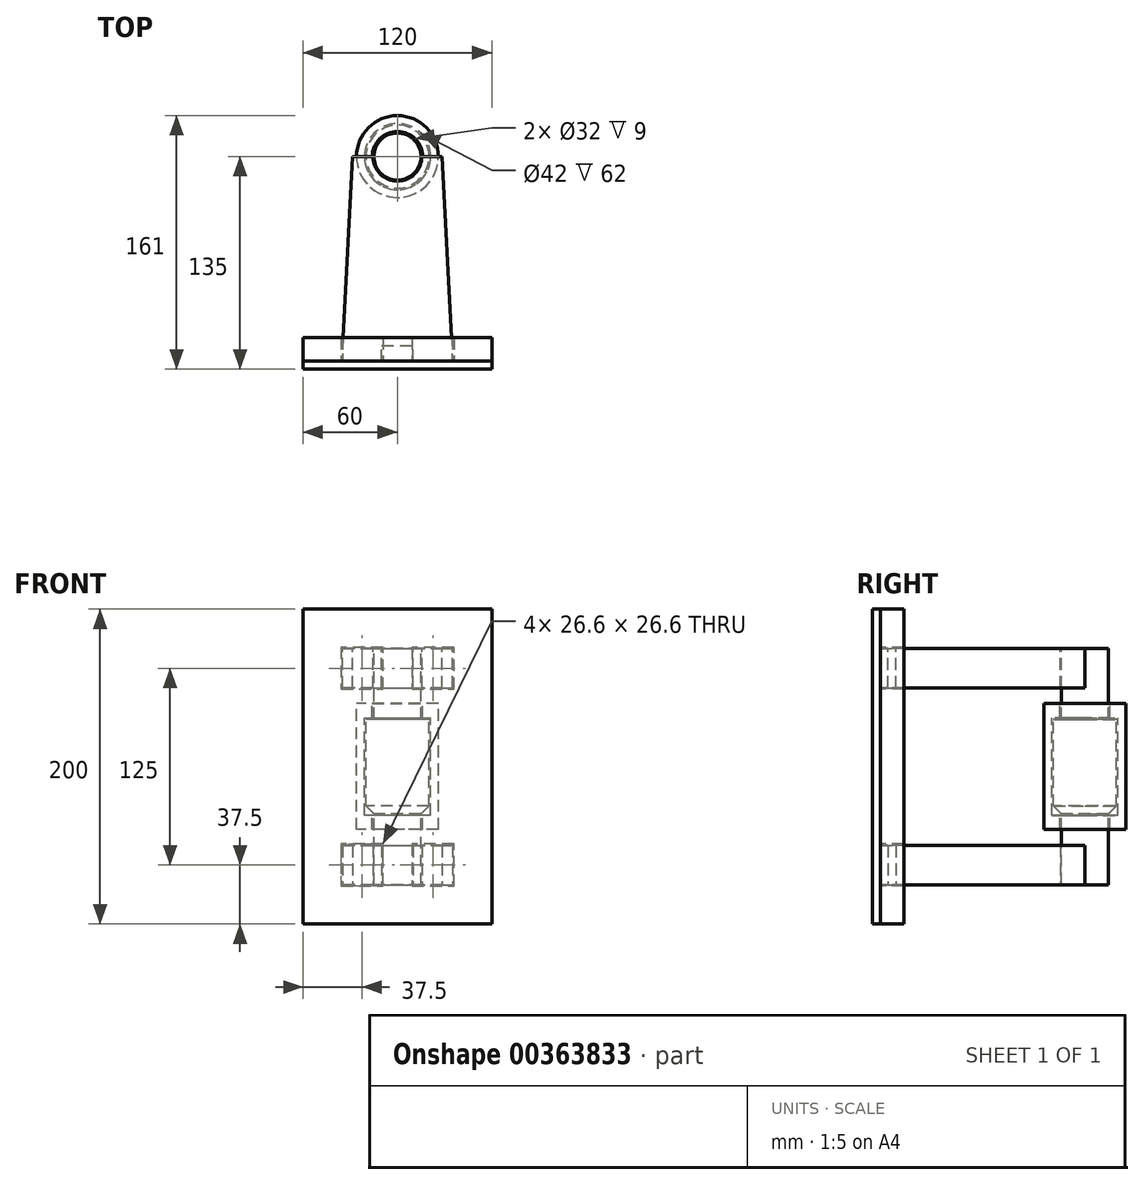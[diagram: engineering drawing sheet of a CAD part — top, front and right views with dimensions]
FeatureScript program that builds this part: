
annotation { "Feature Type Name" : "Feature", "Feature Type Description" : "" }
export const myFeature = defineFeature(function(context is Context, id is Id, definition is map)
    precondition{}
    {
        {
            var Q0;
            Q0=qCreatedBy(makeId("Front.planeOp"),FACE);
            var sketch = newSketch(context, id + "F0", { "sketchPlane" : qUnion([Q0])});
            skLineSegment(sketch, "E0", {"start": v(0, 0) * mm, "end": v(26, 0) * mm});
            skLineSegment(sketch, "E1", {"start": v(26, 0) * mm, "end": v(26, 80) * mm});
            skLineSegment(sketch, "E2", {"start": v(26, 80) * mm, "end": v(0, 80) * mm});
            skLineSegment(sketch, "E3", {"start": v(0, 80) * mm, "end": v(0, 0) * mm});
            skSolve(sketch);
        }
        {
            var Q0;
            Q0=qCreatedBy(makeId("Front.planeOp"),FACE);
            var sketch = newSketch(context, id + "F1", { "sketchPlane" : qUnion([Q0])});
            skLineSegment(sketch, "E4", {"start": v(0, 0) * mm, "end": v(15.4, 0) * mm});
            skLineSegment(sketch, "E5", {"start": v(15, 10) * mm, "end": v(20, 10) * mm});
            skLineSegment(sketch, "E6", {"start": v(20, 10) * mm, "end": v(20, 70) * mm});
            skLineSegment(sketch, "E7", {"start": v(20, 70) * mm, "end": v(15, 70) * mm});
            skLineSegment(sketch, "E8", {"start": v(0, 115) * mm, "end": v(0, -35) * mm});
            skLineSegment(sketch, "E9", {"start": v(0, 115) * mm, "end": v(15, 115) * mm});
            skLineSegment(sketch, "E10", {"start": v(15, 115) * mm, "end": v(15, 70) * mm});
            skLineSegment(sketch, "E11", {"start": v(15, -35) * mm, "end": v(0, -35) * mm});
            skPoint(sketch, "E12.0.end.orphan", {"position": v(0, 80) * mm});
            skLineSegment(sketch, "E13.trimOffspring", {"start": v(15, 10) * mm, "end": v(15, -35) * mm});
            skSolve(sketch);
        }
        {
            var Q0;
            Q0=qSketchRegion(id+"F0",true);
            var Q1;
            Q1=sQuery(id+"F1.wireOp",EDGE,"E8");
            revolve(context, id + "F2", {"entities" : qUnion([Q0]), "axis" : qUnion([Q1]), "revolveType" : RevolveType.FULL});
        }
        {
            var Q0;
            Q0=qSketchRegion(id+"F1",true);
            var Q1;
            Q1=sQuery(id+"F1.wireOp",EDGE,"E8");
            revolve(context, id + "F3", {"entities" : qUnion([Q0]), "axis" : qUnion([Q1]), "revolveType" : RevolveType.FULL});
        }
        {
            var Q0;
            Q0=makeQuery(id+"F3.opRevolve","SWEPT_BODY",BODY,{"disambiguationData":[OSD([sQuery(id+"F1.wireOp",EDGE,"E5"),sQuery(id+"F1.wireOp",EDGE,"E6"),sQuery(id+"F1.wireOp",EDGE,"E7"),sQuery(id+"F1.wireOp",EDGE,"E8"),sQuery(id+"F1.wireOp",EDGE,"E9"),sQuery(id+"F1.wireOp",EDGE,"E10"),sQuery(id+"F1.wireOp",EDGE,"E11"),sQuery(id+"F1.wireOp",EDGE,"E13.trimOffspring")])]});
            var Q1;
            Q1=makeQuery(id+"F2.opRevolve","SWEPT_BODY",BODY,{"disambiguationData":[OSD([sQuery(id+"F0.wireOp",EDGE,"E0"),sQuery(id+"F0.wireOp",EDGE,"E1"),sQuery(id+"F0.wireOp",EDGE,"E2"),sQuery(id+"F0.wireOp",EDGE,"E3")])]});
            booleanBodies(context, id + "F4", {"operationType" : BooleanOperationType.SUBTRACTION, "tools" : qUnion([Q0]), "targets" : qUnion([Q1]), "offset" : true, "offsetAll" : true, "offsetDistance" : 1 * mm, "keepTools" : true});
        }
        {
            var Q0;
            Q0=makeQuery(id+"F3.opRevolve","SWEPT_EDGE",EDGE,{"disambiguationData":[OSD([sQuery(id+"F1.wireOp",EDGE,"E5"),sQuery(id+"F1.wireOp",EDGE,"E6")])]});
            chamfer(context, id + "F5", {"entities" : qUnion([Q0]), "width" : 5 * mm, "tangentPropagation" : true});
        }
        {
            var Q0;
            Q0=makeQuery(id+"F3.opRevolve","SWEPT_FACE",FACE,{"disambiguationData":[OSD([sQuery(id+"F1.wireOp",EDGE,"E9")])]});
            var sketch = newSketch(context, id + "F6", { "sketchPlane" : qUnion([Q0])});
            skLineSegment(sketch, "E14", {"start": v(0, 0) * mm, "end": v(-15, 0) * mm});
            skLineSegment(sketch, "E15", {"start": v(0, 0) * mm, "end": v(15, 0) * mm});
            skLineSegment(sketch, "E16", {"start": v(-15, 0) * mm, "end": v(-35, 0) * mm});
            skLineSegment(sketch, "E17", {"start": v(-35, 0) * mm, "end": v(-35, -130) * mm});
            skLineSegment(sketch, "E18", {"start": v(-35, -130) * mm, "end": v(35, -130) * mm});
            skLineSegment(sketch, "E19", {"start": v(35, -130) * mm, "end": v(35, 0) * mm});
            skLineSegment(sketch, "E20", {"start": v(35, 0) * mm, "end": v(0, 0) * mm});
            skLineSegment(sketch, "E21", {"start": v(28.43, 0) * mm, "end": v(35, -125.14) * mm});
            skLineSegment(sketch, "E22", {"start": v(-28.43, 0) * mm, "end": v(-35, -125.14) * mm});
            skLineSegment(sketch, "E23", {"start": v(0, 0) * mm, "end": v(0, -116.48) * mm, "construction": true});
            skLineSegment(sketch, "E24.bottom", {"start": v(-10, -130) * mm, "end": v(10, -130) * mm});
            skLineSegment(sketch, "E24.top", {"start": v(-10, -120) * mm, "end": v(10, -120) * mm});
            skLineSegment(sketch, "E24.left", {"start": v(-10, -130) * mm, "end": v(-10, -120) * mm});
            skLineSegment(sketch, "E24.right", {"start": v(10, -130) * mm, "end": v(10, -120) * mm});
            skSolve(sketch);
        }
        {
            var Q0;
            {var subQ0=sQuery(id+"F6.wireOp",EDGE,"E18");Q0=makeQuery(id+"F6.imprint","IMPRINT",FACE,{"disambiguationData":[TD([[makeQuery(id+"F6.imprint","IMPRINT",EDGE,{"derivedFrom":subQ0}),1.0]])]});}
            var Q1;
            {var subQ0=sQuery(id+"F6.wireOp",EDGE,"E14");Q1=makeQuery(id+"F6.imprint","IMPRINT",FACE,{"disambiguationData":[TD([[makeQuery(id+"F6.imprint","IMPRINT",EDGE,{"derivedFrom":subQ0}),1.0]])]});}
            extrude(context, id + "F7", {"entities" : qUnion([Q0, Q1]), "oppositeDirection" : true, "depth" : 25 * mm});
        }
        {
            var Q0;
            Q0=makeQuery(id+"F3.opRevolve","SWEPT_BODY",BODY,{"disambiguationData":[OSD([sQuery(id+"F1.wireOp",EDGE,"E5"),sQuery(id+"F1.wireOp",EDGE,"E6"),sQuery(id+"F1.wireOp",EDGE,"E7"),sQuery(id+"F1.wireOp",EDGE,"E8"),sQuery(id+"F1.wireOp",EDGE,"E9"),sQuery(id+"F1.wireOp",EDGE,"E10"),sQuery(id+"F1.wireOp",EDGE,"E11"),sQuery(id+"F1.wireOp",EDGE,"E13.trimOffspring")])]});
            var Q1;
            Q1=makeQuery(id+"F7.opExtrude","SWEPT_BODY",BODY,{"disambiguationData":[OSD([sQuery(id+"F6.wireOp",EDGE,"E14"),sQuery(id+"F6.wireOp",EDGE,"E16"),sQuery(id+"F6.wireOp",EDGE,"E17"),sQuery(id+"F6.wireOp",EDGE,"E18"),sQuery(id+"F6.wireOp",EDGE,"E19"),sQuery(id+"F6.wireOp",EDGE,"E20"),sQuery(id+"F6.wireOp",EDGE,"E21"),sQuery(id+"F6.wireOp",EDGE,"E22")])]});
            booleanBodies(context, id + "F8", {"operationType" : BooleanOperationType.SUBTRACTION, "tools" : qUnion([Q0]), "targets" : qUnion([Q1]), "offset" : true, "offsetAll" : true, "offsetDistance" : .5 * mm, "keepTools" : true});
        }
        {
            var Q0;
            Q0=qCreatedBy(makeId("Top.planeOp"),FACE);
            cPlane(context, id + "F9", {"entities" : qUnion([Q0]), "cplaneType" : CPlaneType.OFFSET, "offset" : 40 * mm, "width" : 150 * mm, "height" : 150 * mm});
        }
        {
            var Q0;
            Q0=makeQuery(id+"F7.opExtrude","SWEPT_BODY",BODY,{"disambiguationData":[OSD([sQuery(id+"F6.wireOp",EDGE,"E14"),sQuery(id+"F6.wireOp",EDGE,"E16"),sQuery(id+"F6.wireOp",EDGE,"E17"),sQuery(id+"F6.wireOp",EDGE,"E18"),sQuery(id+"F6.wireOp",EDGE,"E19"),sQuery(id+"F6.wireOp",EDGE,"E20"),sQuery(id+"F6.wireOp",EDGE,"E21"),sQuery(id+"F6.wireOp",EDGE,"E22"),sQuery(id+"F6.wireOp",EDGE,"E24.top"),sQuery(id+"F6.wireOp",EDGE,"E24.left"),sQuery(id+"F6.wireOp",EDGE,"E24.right")])]});
            var Q1;
            Q1=qCreatedBy(id+"F9.planeOp",FACE);
            mirror(context, id + "F10", {"entities" : qUnion([Q0]), "mirrorPlane" : qUnion([Q1])});
        }
        {
            var Q0;
            {var subQ0=sQuery(id+"F6.wireOp",EDGE,"E18");Q0=makeQuery(id+"F7.opExtrude","SWEPT_FACE",FACE,{"disambiguationData":[OSD([subQ0]),TDD([makeQuery(id+"F6.imprint","IMPRINT",EDGE,{"disambiguationData":[TD([[makeQuery(id+"F6.imprint","INTERSECT",VERTEX,{"derivedFrom":[subQ0,sQuery(id+"F6.wireOp",EDGE,"E19")]}),1.0]])],"derivedFrom":subQ0})])]});}
            var sketch = newSketch(context, id + "F11", { "sketchPlane" : qUnion([Q0])});
            skPoint(sketch, "E25.0", {"position": v(0, 40) * mm});
            skLineSegment(sketch, "E26.bottom", {"start": v(-60, 140) * mm, "end": v(60, 140) * mm});
            skLineSegment(sketch, "E26.top", {"start": v(-60, -60) * mm, "end": v(60, -60) * mm});
            skLineSegment(sketch, "E26.left", {"start": v(-60, 140) * mm, "end": v(-60, -60) * mm});
            skLineSegment(sketch, "E26.right", {"start": v(60, 140) * mm, "end": v(60, -60) * mm});
            skLineSegment(sketch, "E27.0.0", {"start": v(-10, 115) * mm, "end": v(-35, 115) * mm});
            skLineSegment(sketch, "E27.0.1", {"start": v(-35, 115) * mm, "end": v(-35, 90) * mm});
            skLineSegment(sketch, "E27.0.2", {"start": v(-35, 90) * mm, "end": v(-10, 90) * mm});
            skLineSegment(sketch, "E27.0.3", {"start": v(-10, 90) * mm, "end": v(-10, 115) * mm});
            skLineSegment(sketch, "E28.0.0", {"start": v(35, 115) * mm, "end": v(10, 115) * mm});
            skLineSegment(sketch, "E28.0.1", {"start": v(10, 115) * mm, "end": v(10, 90) * mm});
            skLineSegment(sketch, "E28.0.2", {"start": v(10, 90) * mm, "end": v(35, 90) * mm});
            skLineSegment(sketch, "E28.0.3", {"start": v(35, 90) * mm, "end": v(35, 115) * mm});
            skLineSegment(sketch, "E29.0.0", {"start": v(10, -35) * mm, "end": v(35, -35) * mm});
            skLineSegment(sketch, "E29.0.1", {"start": v(35, -35) * mm, "end": v(35, -10) * mm});
            skLineSegment(sketch, "E29.0.2", {"start": v(35, -10) * mm, "end": v(10, -10) * mm});
            skLineSegment(sketch, "E29.0.3", {"start": v(10, -10) * mm, "end": v(10, -35) * mm});
            skLineSegment(sketch, "E30.0.0", {"start": v(-35, -35) * mm, "end": v(-10, -35) * mm});
            skLineSegment(sketch, "E30.0.1", {"start": v(-10, -35) * mm, "end": v(-10, -10) * mm});
            skLineSegment(sketch, "E30.0.2", {"start": v(-10, -10) * mm, "end": v(-35, -10) * mm});
            skLineSegment(sketch, "E30.0.3", {"start": v(-35, -10) * mm, "end": v(-35, -35) * mm});
            skLineSegment(sketch, "E31.0", {"start": v(-9.2, 89.2) * mm, "end": v(-9.2, 115.8) * mm});
            skLineSegment(sketch, "E31.1", {"start": v(-35.8, 89.2) * mm, "end": v(-9.2, 89.2) * mm});
            skLineSegment(sketch, "E31.2", {"start": v(-35.8, 115.8) * mm, "end": v(-35.8, 89.2) * mm});
            skLineSegment(sketch, "E31.3", {"start": v(-9.2, 115.8) * mm, "end": v(-35.8, 115.8) * mm});
            skLineSegment(sketch, "E32.0", {"start": v(9.2, 115.8) * mm, "end": v(9.2, 89.2) * mm});
            skLineSegment(sketch, "E32.1", {"start": v(35.8, 115.8) * mm, "end": v(9.2, 115.8) * mm});
            skLineSegment(sketch, "E32.2", {"start": v(35.8, 89.2) * mm, "end": v(35.8, 115.8) * mm});
            skLineSegment(sketch, "E32.3", {"start": v(9.2, 89.2) * mm, "end": v(35.8, 89.2) * mm});
            skLineSegment(sketch, "E33.0", {"start": v(9.2, -9.2) * mm, "end": v(9.2, -35.8) * mm});
            skLineSegment(sketch, "E33.1", {"start": v(35.8, -9.2) * mm, "end": v(9.2, -9.2) * mm});
            skLineSegment(sketch, "E33.2", {"start": v(35.8, -35.8) * mm, "end": v(35.8, -9.2) * mm});
            skLineSegment(sketch, "E33.3", {"start": v(9.2, -35.8) * mm, "end": v(35.8, -35.8) * mm});
            skLineSegment(sketch, "E34.0", {"start": v(-35.8, -35.8) * mm, "end": v(-9.2, -35.8) * mm});
            skLineSegment(sketch, "E34.1", {"start": v(-35.8, -9.2) * mm, "end": v(-35.8, -35.8) * mm});
            skLineSegment(sketch, "E34.2", {"start": v(-9.2, -9.2) * mm, "end": v(-35.8, -9.2) * mm});
            skLineSegment(sketch, "E34.3", {"start": v(-9.2, -35.8) * mm, "end": v(-9.2, -9.2) * mm});
            skSolve(sketch);
        }
        {
            var Q0;
            Q0=makeQuery(id+"F11.imprint","IMPRINT",FACE,{"disambiguationData":[TD([[makeQuery(id+"F11.imprint","IMPRINT",EDGE,{"derivedFrom":sQuery(id+"F11.wireOp",EDGE,"E26.bottom")}),-1.0]])]});
            extrude(context, id + "F12", {"entities" : qUnion([Q0]), "oppositeDirection" : true, "depth" : 15 * mm});
        }
        {
            var Q0;
            Q0=makeQuery(id+"F11.imprint","IMPRINT",FACE,{"disambiguationData":[TD([[makeQuery(id+"F11.imprint","IMPRINT",EDGE,{"derivedFrom":sQuery(id+"F11.wireOp",EDGE,"E26.bottom")}),-1.0]])]});
            var Q1;
            Q1=makeQuery(id+"F11.imprint","IMPRINT",FACE,{"disambiguationData":[TD([[makeQuery(id+"F11.imprint","IMPRINT",EDGE,{"derivedFrom":sQuery(id+"F11.wireOp",EDGE,"E27.0.0")}),1.0]])]});
            var Q2;
            Q2=makeQuery(id+"F11.imprint","IMPRINT",FACE,{"disambiguationData":[TD([[makeQuery(id+"F11.imprint","IMPRINT",EDGE,{"derivedFrom":sQuery(id+"F11.wireOp",EDGE,"E28.0.0")}),-1.0]])]});
            var Q3;
            Q3=makeQuery(id+"F11.imprint","IMPRINT",FACE,{"disambiguationData":[TD([[makeQuery(id+"F11.imprint","IMPRINT",EDGE,{"derivedFrom":sQuery(id+"F11.wireOp",EDGE,"E29.0.0")}),1.0]])]});
            var Q4;
            Q4=makeQuery(id+"F11.imprint","IMPRINT",FACE,{"disambiguationData":[TD([[makeQuery(id+"F11.imprint","IMPRINT",EDGE,{"derivedFrom":sQuery(id+"F11.wireOp",EDGE,"E30.0.0")}),1.0]])]});
            var Q5;
            Q5=makeQuery(id+"F11.imprint","IMPRINT",FACE,{"disambiguationData":[TD([[makeQuery(id+"F11.imprint","IMPRINT",EDGE,{"derivedFrom":sQuery(id+"F11.wireOp",EDGE,"E29.0.0")}),-1.0]])]});
            var Q6;
            Q6=makeQuery(id+"F11.imprint","IMPRINT",FACE,{"disambiguationData":[TD([[makeQuery(id+"F11.imprint","IMPRINT",EDGE,{"derivedFrom":sQuery(id+"F11.wireOp",EDGE,"E30.0.0")}),-1.0]])]});
            var Q7;
            {var subQ0=sQuery(id+"F1.wireOp",EDGE,"E5");Q7=makeQuery(id+"F1.imprint","IMPRINT",FACE,{"disambiguationData":[TD([[makeQuery(id+"F1.imprint","IMPRINT",EDGE,{"derivedFrom":subQ0}),1.0]])]});}
            var Q8;
            {var subQ5=sQuery(id+"F1.wireOp",EDGE,"E11");Q8=makeQuery(id+"F1.imprint","IMPRINT",FACE,{"disambiguationData":[TD([[makeQuery(id+"F1.imprint","IMPRINT",EDGE,{"derivedFrom":subQ5}),-1.0]])]});}
            var Q9;
            Q9=makeQuery(id+"F11.imprint","IMPRINT",FACE,{"disambiguationData":[TD([[makeQuery(id+"F11.imprint","IMPRINT",EDGE,{"derivedFrom":sQuery(id+"F11.wireOp",EDGE,"E27.0.0")}),-1.0]])]});
            var Q10;
            Q10=makeQuery(id+"F11.imprint","IMPRINT",FACE,{"disambiguationData":[TD([[makeQuery(id+"F11.imprint","IMPRINT",EDGE,{"derivedFrom":sQuery(id+"F11.wireOp",EDGE,"E28.0.0")}),1.0]])]});
            extrude(context, id + "F13", {"entities" : qUnion([Q0, Q1, Q2, Q3, Q4, Q5, Q6, Q7, Q8, Q9, Q10]), "depth" : 5 * mm});
        }
        {
            var Q0;
            Q0=makeQuery(id+"F13.opExtrude","SWEPT_BODY",BODY,{"disambiguationData":[OSD([sQuery(id+"F1.wireOp",EDGE,"E5"),sQuery(id+"F1.wireOp",EDGE,"E6"),sQuery(id+"F1.wireOp",EDGE,"E7"),sQuery(id+"F1.wireOp",EDGE,"E8"),sQuery(id+"F1.wireOp",EDGE,"E9"),sQuery(id+"F1.wireOp",EDGE,"E10"),sQuery(id+"F1.wireOp",EDGE,"E11"),sQuery(id+"F1.wireOp",EDGE,"E13.trimOffspring")])]});
            deleteBodies(context, id + "F14", {"entities" : qUnion([Q0])});
        }
    });
